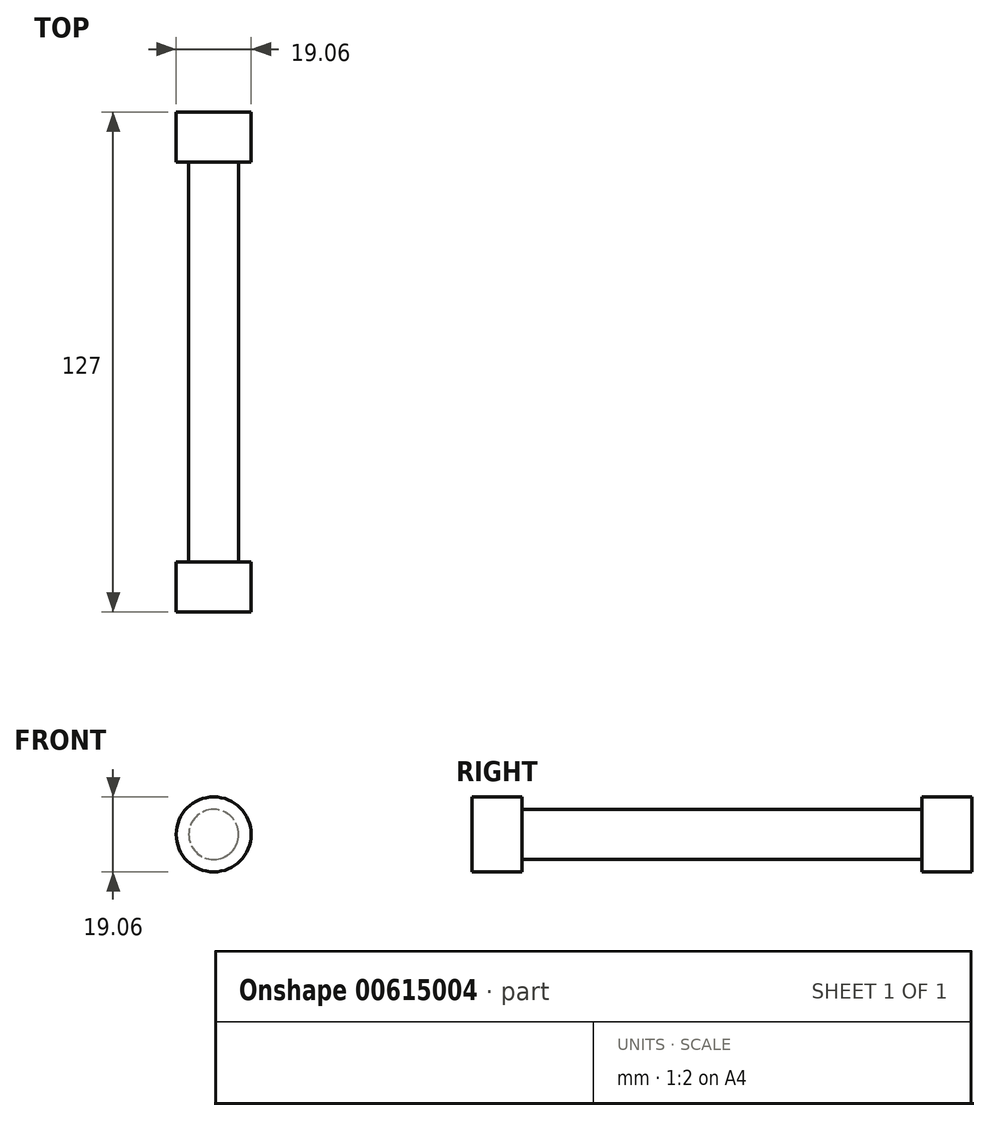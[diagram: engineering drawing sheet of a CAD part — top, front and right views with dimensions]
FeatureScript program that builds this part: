
annotation { "Feature Type Name" : "Feature", "Feature Type Description" : "" }
export const myFeature = defineFeature(function(context is Context, id is Id, definition is map)
    precondition{}
    {
        {
            var Q0;
            Q0=qCreatedBy(makeId("Front.planeOp"),FACE);
            var sketch = newSketch(context, id + "F0", { "sketchPlane" : qUnion([Q0])});
            skCircle(sketch, "E0", {"center": v(0, 0) * mm, "radius": 6.35 * mm});
            skSolve(sketch);
        }
        {
            var Q0;
            Q0=makeQuery(id+"F0.imprint","IMPRINT",FACE,{"disambiguationData":[TD([[makeQuery(id+"F0.imprint","IMPRINT",EDGE,{"derivedFrom":sQuery(id+"F0.wireOp",EDGE,"E0")}),1.0]])]});
            extrude(context, id + "F1", {"entities" : qUnion([Q0]), "endBound" : BoundingType.SYMMETRIC, "depth" : 127 * mm, "offsetDistance" : 25.4 * mm});
        }
        {
            var Q0;
            Q0=makeQuery(id+"F1.opExtrude","CAP_FACE",FACE,{"disambiguationData":[OSD([sQuery(id+"F0.wireOp",EDGE,"E0")])],"isStart":false});
            var sketch = newSketch(context, id + "F2", { "sketchPlane" : qUnion([Q0])});
            skCircle(sketch, "E1", {"center": v(0, 0) * mm, "radius": 9.53 * mm});
            skSolve(sketch);
        }
        {
            var Q0;
            Q0=makeQuery(id+"F1.opExtrude","CAP_FACE",FACE,{"disambiguationData":[OSD([sQuery(id+"F0.wireOp",EDGE,"E0")])],"isStart":true});
            var sketch = newSketch(context, id + "F3", { "sketchPlane" : qUnion([Q0])});
            skCircle(sketch, "E2", {"center": v(0, 0) * mm, "radius": 9.53 * mm});
            skSolve(sketch);
        }
        {
            var Q0;
            Q0=makeQuery(id+"F3.imprint","IMPRINT",FACE,{"disambiguationData":[TD([[makeQuery(id+"F3.imprint","IMPRINT",EDGE,{"derivedFrom":sQuery(id+"F3.wireOp",EDGE,"E2")}),1.0]])]});
            extrude(context, id + "F4", {"entities" : qUnion([Q0]), "operationType" : NewBodyOperationType.ADD, "oppositeDirection" : true, "depth" : 12.7 * mm, "offsetDistance" : 25.4 * mm});
        }
        {
            var Q0;
            Q0=makeQuery(id+"F2.imprint","IMPRINT",FACE,{"disambiguationData":[TD([[makeQuery(id+"F2.imprint","IMPRINT",EDGE,{"derivedFrom":sQuery(id+"F2.wireOp",EDGE,"E1")}),1.0]])]});
            extrude(context, id + "F5", {"entities" : qUnion([Q0]), "operationType" : NewBodyOperationType.ADD, "oppositeDirection" : true, "depth" : 12.7 * mm, "offsetDistance" : 25.4 * mm});
        }
    });
